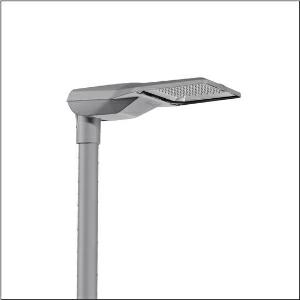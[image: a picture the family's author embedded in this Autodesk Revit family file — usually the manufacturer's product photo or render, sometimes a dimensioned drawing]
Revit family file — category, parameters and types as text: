
# Revit family: streetlight_sl_21_iq_midi___st0_8a_5xe3c41g08nb_9f8f
name_source: partatom
category: Lighting Fixtures
units: mm (PartAtom-declared; Revit-internal decimal feet)

## family parameters
Cut with Voids When Loaded = No
Host = Face
Light Source = No
Part Type = Normal
Room Calculation Point = No
Round Connector Dimension = Use Diameter
Shared = No

## types (1)
- --- (1 x LED, 24250 lm, 155.5 W, 4000K)
    Apparent Load = 155 VA
    CIE Flux Codes = 41 75 97 100 100
    Color Rendering = 70
    Color Temperature = 4000K
    Default Elevation = 1800 mm
    Description = Streetlight SL 21 iQ midi, mast luminaire, primary light control with lens, of PMMA, primary optical cover: cover, of toughened safety glass, transparent, light distribution: ST0.8a, light emission: direct distribution, primary light characteristic: asymmetric, installation type: post-top, side-entry, LED, High Power LED, rated luminous flux: 24.250lm, luminous efficacy: 156lm/W, light colour: 740, colour temperature: 4000K, control: Street-Remote, Auto-Match, Temp-Guard, Lumen-Switch, Night-Set, Smart-Wire, Light-Fading, Desk-Remote (wireless, voltage-free reading and setting of iQ features in the workshop via application-optimized NFC function/RFID function), optimised constant luminous flux control (CLO 2.0), presetting dimming linear, mains connection: 230..240V, AC, 50/60Hz, start of lifetime: 156W, end of service life: 162W, reduction: 69W, luminaire housing, of diecast aluminium, powder-coated, Siteco® metallic grey (DB 702S), corrosivity category C5 mid according to DIN EN ISO 12944, please order mast flange separately, inclination adjustable: 0°, 5°, 10°, 15°, sealing non-destructively replaceable, multi-level sealing system, length: 644mm, width: 335mm, height: 110mm, mast flange for spigot size: 42mm (side-entry): 5XC10008XM4, 60/48mm (side-entry/post-top): 5XC10108XM2, 76/60mm (side-entry/post-top): 5XC10108XM1, protection rating (complete): IP66, insulation class (complete): insulation class II (safety insulation), certification: CE, ENEC, ENEC+, VDE, impact resistance: IK09, permissible operating ambient temperature for outdoor applications: -40..+50°C, standard-compliant lighting for roads and squares, packaging unit: 1 piece

Light Distribution: ST0.8a
    Height = 111 mm
    Lamp = 1 x LED
    Lamp Light Flux = 24250 lm
    Lamp Power = 155.5 W
    Lamp count = 1
    Length = 644 mm
    Luminous efficacy = 156 lm/W
    Manufacturer = Siteco
    ModVariant = No
    Model = 5XE3C41G08NB
    Number of Poles = 1
    OnlyDefault = Yes
    Power Factor = 1
    Product Name = Streetlight SL 21 iQ midi | ST0.8a
    Product group = mast luminaire | pylon top
    ProductGroupID = 6100
    Protection Class = Protection class II
    Protection Degree = IP 66
    RLX_Detail_Level = 1
    RLX_Emergency_Light_Flux = 0 lm
    RLX_Emergency_Type = 0
    RLX_Emergency_Type_DB = No
    RlxData = <blob elided: 90649 chars, md5=965e3f9b>
    Socket = socket
    Standby Power = 0 W
    System Light Flux = 24250 lm
    System Power = 155 W
    Type Comments = factory setting: luminous flux: 100 % | dim-lin: 254 | 823 mA
    Type Image = l_1004298.jpg
    URL = http://relux.com
    VarID = @adj_101305
    Voltage = 0 V
    Weight = 0.00 kg
    Width = 336 mm

## geometry (parser evidence)
native form markers: Blend x4, Sweep x12
no freeform markers — native parametric forms only
